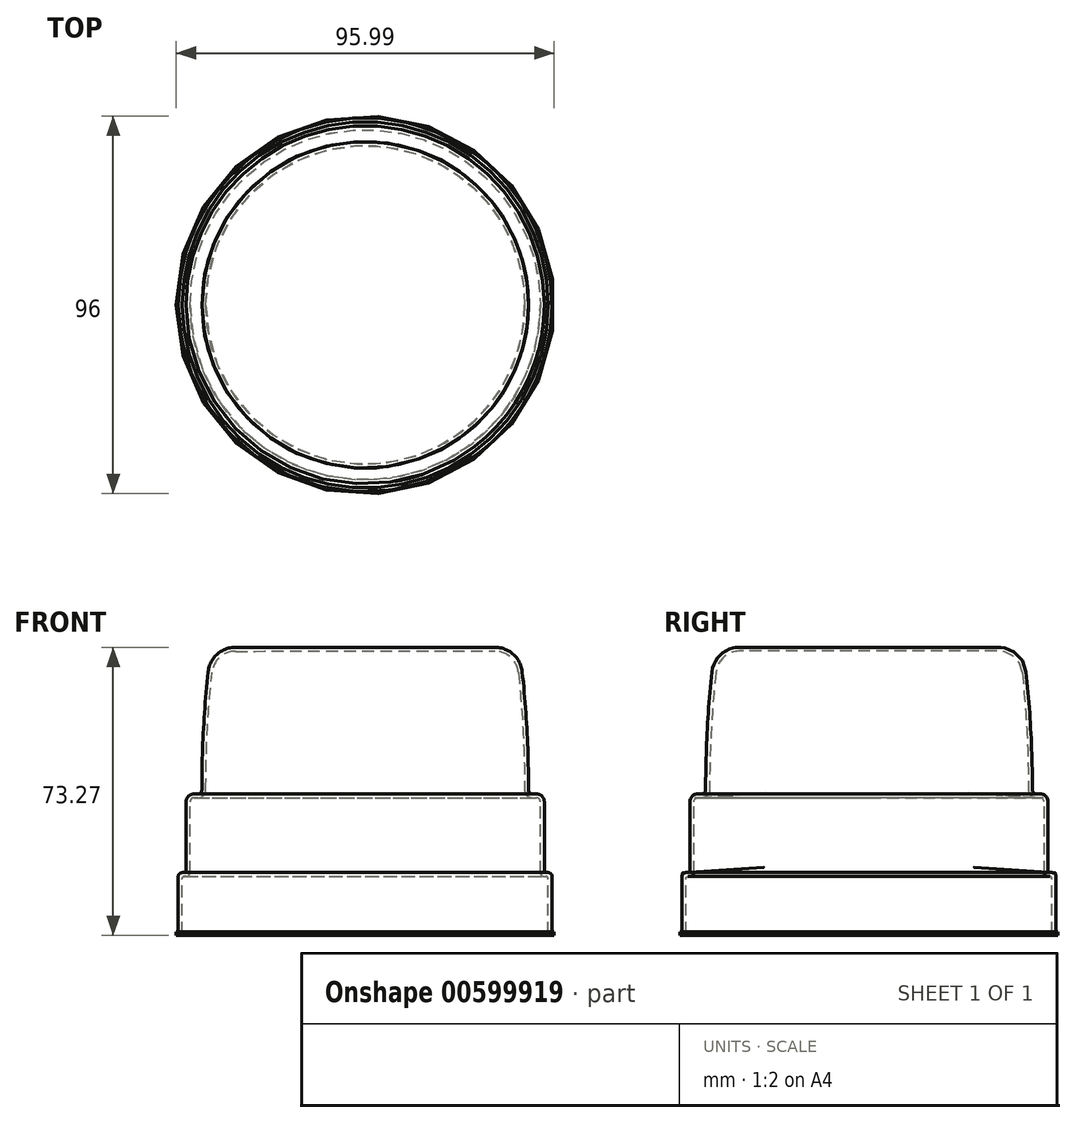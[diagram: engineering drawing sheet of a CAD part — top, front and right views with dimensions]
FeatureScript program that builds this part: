
annotation { "Feature Type Name" : "Feature", "Feature Type Description" : "" }
export const myFeature = defineFeature(function(context is Context, id is Id, definition is map)
    precondition{}
    {
        {
            var Q0;
            Q0=qCreatedBy(makeId("Front.planeOp"),FACE);
            var sketch = newSketch(context, id + "F0", { "sketchPlane" : qUnion([Q0])});
            skLineSegment(sketch, "E0", {"start": v(46.5, -4.5) * mm, "end": v(46.5, 9.5) * mm});
            skLineSegment(sketch, "E1", {"start": v(46, 10) * mm, "end": v(45.5, 10) * mm});
            skLineSegment(sketch, "E2", {"start": v(44.5, 11) * mm, "end": v(44.5, 29) * mm});
            skLineSegment(sketch, "E3", {"start": v(43.5, 30) * mm, "end": v(42.5, 30) * mm});
            skLineSegment(sketch, "E4.2", {"start": v(47.5, -4) * mm, "end": v(47.5, 10) * mm});
            skLineSegment(sketch, "E4.3", {"start": v(46.5, 11) * mm, "end": v(46, 11) * mm});
            skLineSegment(sketch, "E4.4", {"start": v(45.5, 11.5) * mm, "end": v(45.5, 29) * mm});
            skLineSegment(sketch, "E4.5", {"start": v(43.5, 31) * mm, "end": v(42.5, 31) * mm});
            skPoint(sketch, "E5.visualSharp", {"position": v(40.5, 75) * mm});
            skPoint(sketch, "E6.visualSharp", {"position": v(46.5, 10) * mm});
            skArc(sketch, "E6.filletArc", {"start": v(46.5, 9.5) * mm, "mid": v(46.35, 9.85) * mm, "end": v(46, 10) * mm});
            skPoint(sketch, "E7.visualSharp", {"position": v(44.5, 10) * mm});
            skArc(sketch, "E7.filletArc", {"start": v(44.5, 11) * mm, "mid": v(44.8, 10.3) * mm, "end": v(45.5, 10) * mm});
            skArc(sketch, "E8.filletArc", {"start": v(45.5, 11.5) * mm, "mid": v(45.65, 11.15) * mm, "end": v(46, 11) * mm});
            skPoint(sketch, "E9.visualSharp", {"position": v(47.5, 11) * mm});
            skArc(sketch, "E9.filletArc", {"start": v(47.5, 10) * mm, "mid": v(47.2, 10.7) * mm, "end": v(46.5, 11) * mm});
            skPoint(sketch, "E10.visualSharp", {"position": v(44.5, 30) * mm});
            skArc(sketch, "E10.filletArc", {"start": v(44.5, 29) * mm, "mid": v(44.2, 29.7) * mm, "end": v(43.5, 30) * mm});
            skPoint(sketch, "E11.visualSharp", {"position": v(40.5, 30) * mm});
            skArc(sketch, "E11.filletArc", {"start": v(40.5, 32) * mm, "mid": v(41.09, 30.59) * mm, "end": v(42.5, 30) * mm});
            skPoint(sketch, "E12.visualSharp", {"position": v(45.5, 31) * mm});
            skArc(sketch, "E12.filletArc", {"start": v(45.5, 29) * mm, "mid": v(44.91, 30.41) * mm, "end": v(43.5, 31) * mm});
            skPoint(sketch, "E13.visualSharp", {"position": v(41.5, 31) * mm});
            skArc(sketch, "E13.filletArc", {"start": v(41.5, 32) * mm, "mid": v(41.8, 31.3) * mm, "end": v(42.5, 31) * mm});
            skLineSegment(sketch, "E14", {"start": v(47, -5) * mm, "end": v(48, -5) * mm});
            skLineSegment(sketch, "E15", {"start": v(48, -5) * mm, "end": v(48, -4) * mm});
            skLineSegment(sketch, "E16", {"start": v(48, -4) * mm, "end": v(47.5, -4) * mm});
            skPoint(sketch, "E17.visualSharp", {"position": v(46.5, -5) * mm});
            skArc(sketch, "E17.filletArc", {"start": v(46.5, -4.5) * mm, "mid": v(46.65, -4.85) * mm, "end": v(47, -5) * mm});
            skArc(sketch, "E18", {"start": v(41.5, 32) * mm, "mid": v(41.1, 47.02) * mm, "end": v(39.9, 62) * mm});
            skArc(sketch, "E19.filletArc", {"start": v(39.9, 62) * mm, "mid": v(37.62, 66.46) * mm, "end": v(32.94, 68.26) * mm});
            skArc(sketch, "E20.0", {"start": v(38.9, 61.9) * mm, "mid": v(36.95, 65.72) * mm, "end": v(32.94, 67.26) * mm});
            skArc(sketch, "E20.1", {"start": v(40.5, 32) * mm, "mid": v(40.1, 46.97) * mm, "end": v(38.9, 61.9) * mm});
            skLineSegment(sketch, "E21", {"start": v(32.94, 67.26) * mm, "end": v(0, 67.25) * mm});
            skLineSegment(sketch, "E22", {"start": v(0, 67.25) * mm, "end": v(0, 68.26) * mm});
            skLineSegment(sketch, "E23", {"start": v(0, 68.26) * mm, "end": v(32.94, 68.26) * mm});
            skPoint(sketch, "E24.start.orphan", {"position": v(0, 75) * mm});
            skSolve(sketch);
        }
        {
            var Q0;
            Q0=makeQuery(id+"F0.imprint","IMPRINT",FACE,{"disambiguationData":[TD([[makeQuery(id+"F0.imprint","IMPRINT",EDGE,{"derivedFrom":sQuery(id+"F0.wireOp",EDGE,"E0")}),-1.0]])]});
            var Q1;
            Q1=sQuery(id+"F0.wireOp",EDGE,"E22");
            revolve(context, id + "F1", {"entities" : qUnion([Q0]), "axis" : qUnion([Q1]), "revolveType" : RevolveType.FULL});
        }
    });
